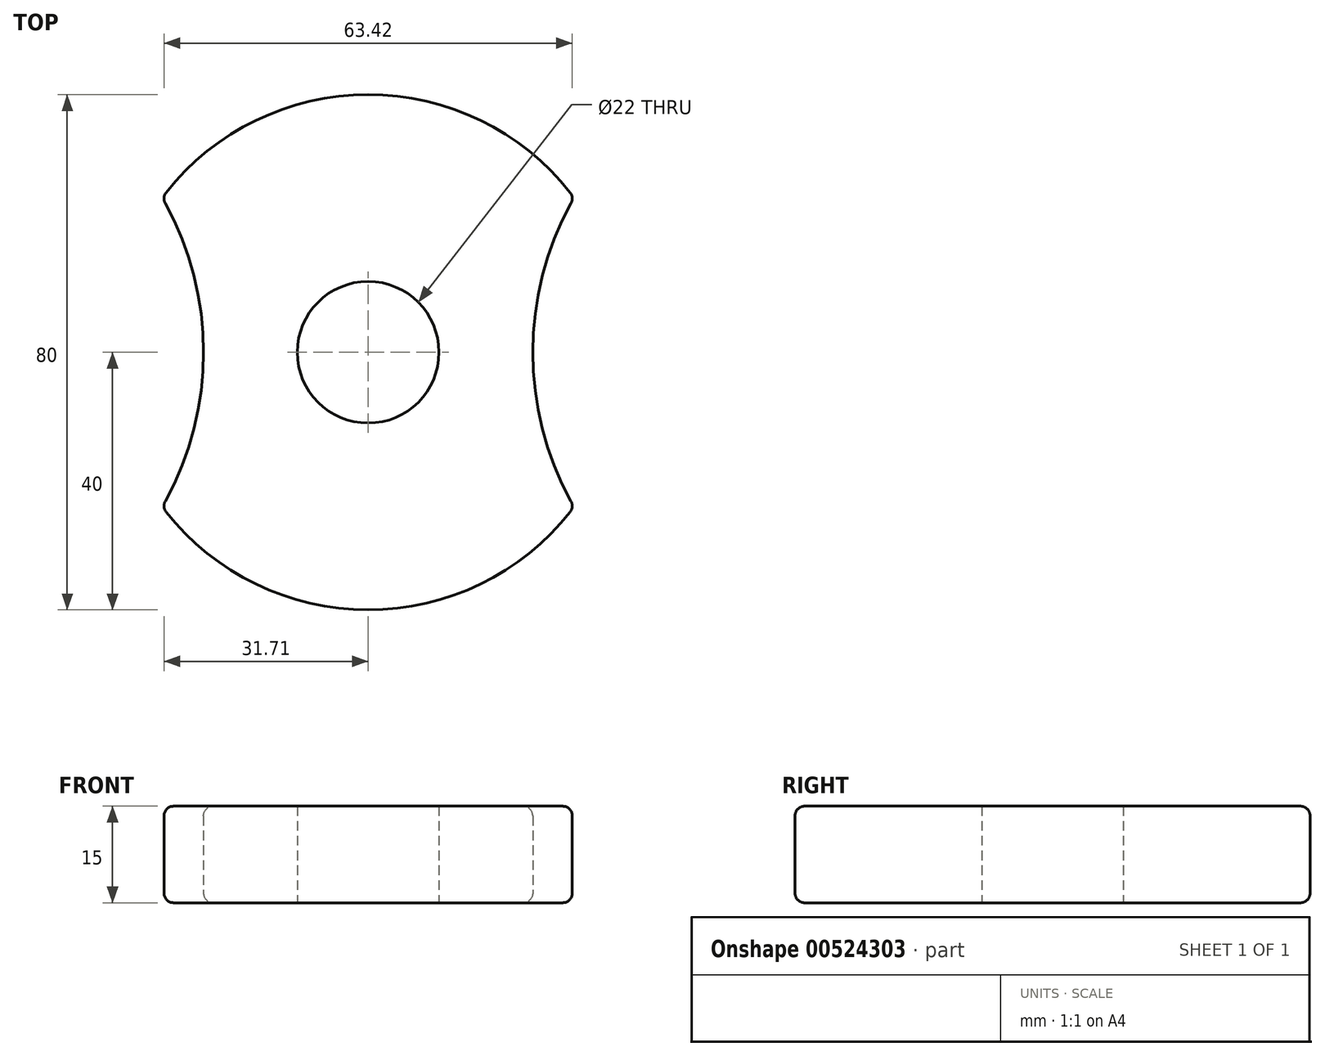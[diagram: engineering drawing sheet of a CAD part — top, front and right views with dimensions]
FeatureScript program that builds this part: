
annotation { "Feature Type Name" : "Feature", "Feature Type Description" : "" }
export const myFeature = defineFeature(function(context is Context, id is Id, definition is map)
    precondition{}
    {
        {
            var Q0;
            Q0=qCreatedBy(makeId("Top.planeOp"),FACE);
            var sketch = newSketch(context, id + "F0", { "sketchPlane" : qUnion([Q0])});
            skArc(sketch, "E0", {"start": v(-32, -24) * mm, "mid": v(0, -40) * mm, "end": v(32, -24) * mm});
            skLineSegment(sketch, "E1.bottom", {"start": v(32, -24) * mm, "end": v(-32, -24) * mm, "construction": true});
            skLineSegment(sketch, "E1.top", {"start": v(32, 24) * mm, "end": v(-32, 24) * mm, "construction": true});
            skLineSegment(sketch, "E1.left", {"start": v(32, -24) * mm, "end": v(32, 24) * mm, "construction": true});
            skLineSegment(sketch, "E1.right", {"start": v(-32, -24) * mm, "end": v(-32, 24) * mm, "construction": true});
            skLineSegment(sketch, "E2", {"start": v(32, 24) * mm, "end": v(73.57, 0) * mm, "construction": true});
            skLineSegment(sketch, "E3", {"start": v(73.57, 0) * mm, "end": v(32, -24) * mm, "construction": true});
            skArc(sketch, "E4", {"start": v(32, 24) * mm, "mid": v(25.57, 0) * mm, "end": v(32, -24) * mm});
            skLineSegment(sketch, "E5", {"start": v(-32, 24) * mm, "end": v(-73.57, 0) * mm, "construction": true});
            skLineSegment(sketch, "E6", {"start": v(-73.57, 0) * mm, "end": v(-32, -24) * mm, "construction": true});
            skArc(sketch, "E7", {"start": v(-32, -24) * mm, "mid": v(-25.57, 0) * mm, "end": v(-32, 24) * mm});
            skArc(sketch, "E8.trimOffspring", {"start": v(32, 24) * mm, "mid": v(0, 40) * mm, "end": v(-32, 24) * mm});
            skCircle(sketch, "E9", {"center": v(0, 0) * mm, "radius": 11 * mm});
            skSolve(sketch);
        }
        {
            var Q0;
            Q0=makeQuery(id+"F0.imprint","IMPRINT",FACE,{"disambiguationData":[TD([[makeQuery(id+"F0.imprint","IMPRINT",EDGE,{"derivedFrom":sQuery(id+"F0.wireOp",EDGE,"E0")}),1.0]])]});
            extrude(context, id + "F1", {"entities" : qUnion([Q0]), "depth" : 15 * mm, "offsetDistance" : 25 * mm});
        }
        {
            var Q0;
            Q0=makeQuery(id+"F1.opExtrude","SWEPT_FACE",FACE,{"disambiguationData":[OSD([sQuery(id+"F0.wireOp",EDGE,"E0")])]});
            var Q1;
            Q1=makeQuery(id+"F1.opExtrude","SWEPT_FACE",FACE,{"disambiguationData":[OSD([sQuery(id+"F0.wireOp",EDGE,"E4")])]});
            var Q2;
            Q2=makeQuery(id+"F1.opExtrude","SWEPT_FACE",FACE,{"disambiguationData":[OSD([sQuery(id+"F0.wireOp",EDGE,"E8.trimOffspring")])]});
            var Q3;
            Q3=makeQuery(id+"F1.opExtrude","SWEPT_FACE",FACE,{"disambiguationData":[OSD([sQuery(id+"F0.wireOp",EDGE,"E7")])]});
            fillet(context, id + "F2", {"entities" : qUnion([Q0, Q1, Q2, Q3]), "radius" : 1.5 * mm, "tangentPropagation" : true, "allowEdgeOverflow" : false});
        }
    });
